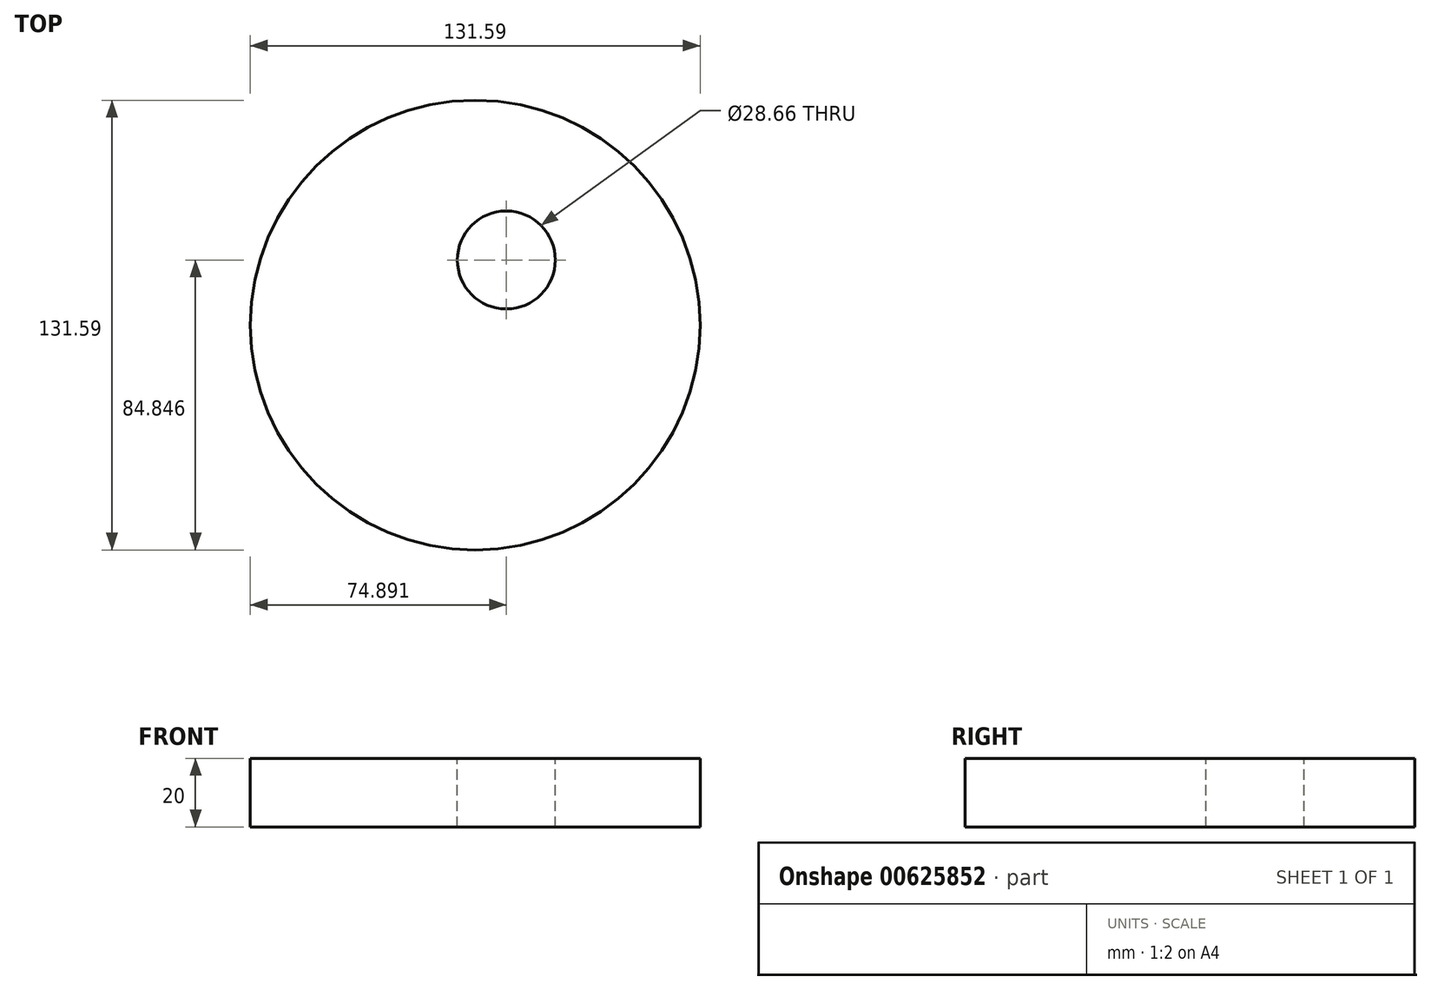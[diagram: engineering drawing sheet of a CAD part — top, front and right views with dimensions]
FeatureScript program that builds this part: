
annotation { "Feature Type Name" : "Feature", "Feature Type Description" : "" }
export const myFeature = defineFeature(function(context is Context, id is Id, definition is map)
    precondition{}
    {
        {
            var Q0;
            Q0=qCreatedBy(makeId("Top.planeOp"),FACE);
            var sketch = newSketch(context, id + "F0", { "sketchPlane" : qUnion([Q0])});
            skCircle(sketch, "E0", {"center": v(-45.04, -33.16) * mm, "radius": 65.8 * mm});
            skSolve(sketch);
        }
        {
            var Q0;
            Q0=makeQuery(id+"F0.imprint","IMPRINT",FACE,{"disambiguationData":[TD([[makeQuery(id+"F0.imprint","IMPRINT",EDGE,{"derivedFrom":sQuery(id+"F0.wireOp",EDGE,"E0")}),1.0]])]});
            extrude(context, id + "F1", {"entities" : qUnion([Q0]), "depth" : 20 * mm, "offsetDistance" : 25.4 * mm});
        }
        {
            var Q0;
            Q0=makeQuery(id+"F1.opExtrude","CAP_FACE",FACE,{"disambiguationData":[OSD([sQuery(id+"F0.wireOp",EDGE,"E0")])],"isStart":false});
            var sketch = newSketch(context, id + "F2", { "sketchPlane" : qUnion([Q0])});
            skCircle(sketch, "E1", {"center": v(-84.16, -47.35) * mm, "radius": 15.14 * mm});
            skCircle(sketch, "E2", {"center": v(-35.95, -14.11) * mm, "radius": 14.33 * mm});
            skSolve(sketch);
        }
        {
            var Q0;
            Q0=makeQuery(id+"F2.imprint","IMPRINT",FACE,{"disambiguationData":[TD([[makeQuery(id+"F2.imprint","IMPRINT",EDGE,{"derivedFrom":sQuery(id+"F2.wireOp",EDGE,"E2")}),1.0]])]});
            extrude(context, id + "F3", {"entities" : qUnion([Q0]), "operationType" : NewBodyOperationType.REMOVE, "oppositeDirection" : true, "depth" : 59.94 * mm, "offsetDistance" : 25.4 * mm});
        }
    });
